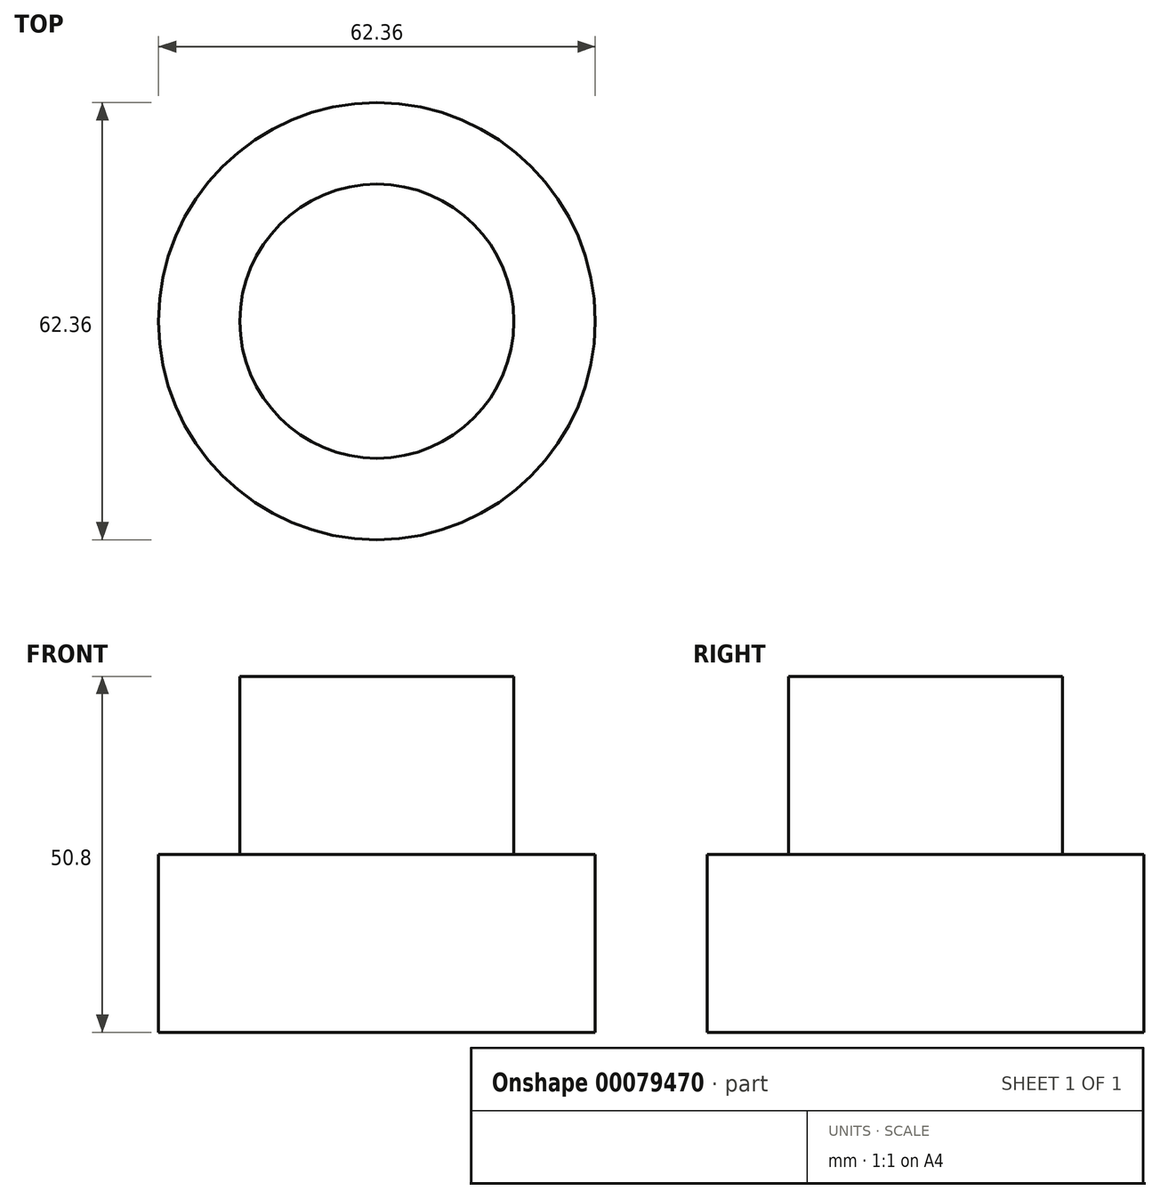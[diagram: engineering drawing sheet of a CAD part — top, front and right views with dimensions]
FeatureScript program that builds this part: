
annotation { "Feature Type Name" : "Feature", "Feature Type Description" : "" }
export const myFeature = defineFeature(function(context is Context, id is Id, definition is map)
    precondition{}
    {
        {
            var Q0;
            Q0=qCreatedBy(makeId("Top.planeOp"),FACE);
            var sketch = newSketch(context, id + "F0", { "sketchPlane" : qUnion([Q0])});
            skCircle(sketch, "E0", {"center": v(0, 0) * mm, "radius": 19.56 * mm});
            skSolve(sketch);
        }
        {
            var Q0;
            Q0=makeQuery(id+"F0.imprint","IMPRINT",FACE,{"disambiguationData":[TD([[makeQuery(id+"F0.imprint","IMPRINT",EDGE,{"derivedFrom":sQuery(id+"F0.wireOp",EDGE,"E0")}),1.0]])]});
            extrude(context, id + "F1", {"entities" : qUnion([Q0]), "depth" : 25.4 * mm});
        }
        {
            var Q0;
            Q0=makeQuery(id+"F1.opExtrude","CAP_FACE",FACE,{"disambiguationData":[OSD([sQuery(id+"F0.wireOp",EDGE,"E0")])],"isStart":true});
            var sketch = newSketch(context, id + "F2", { "sketchPlane" : qUnion([Q0])});
            skCircle(sketch, "E1", {"center": v(0, 0) * mm, "radius": 31.18 * mm});
            skSolve(sketch);
        }
        {
            var Q0;
            Q0 = qSketchRegion(id + "F2", true);
            extrude(context, id + "F3", {"entities" : qUnion([Q0]), "operationType" : NewBodyOperationType.ADD, "depth" : 25.4 * mm});
        }
    });
